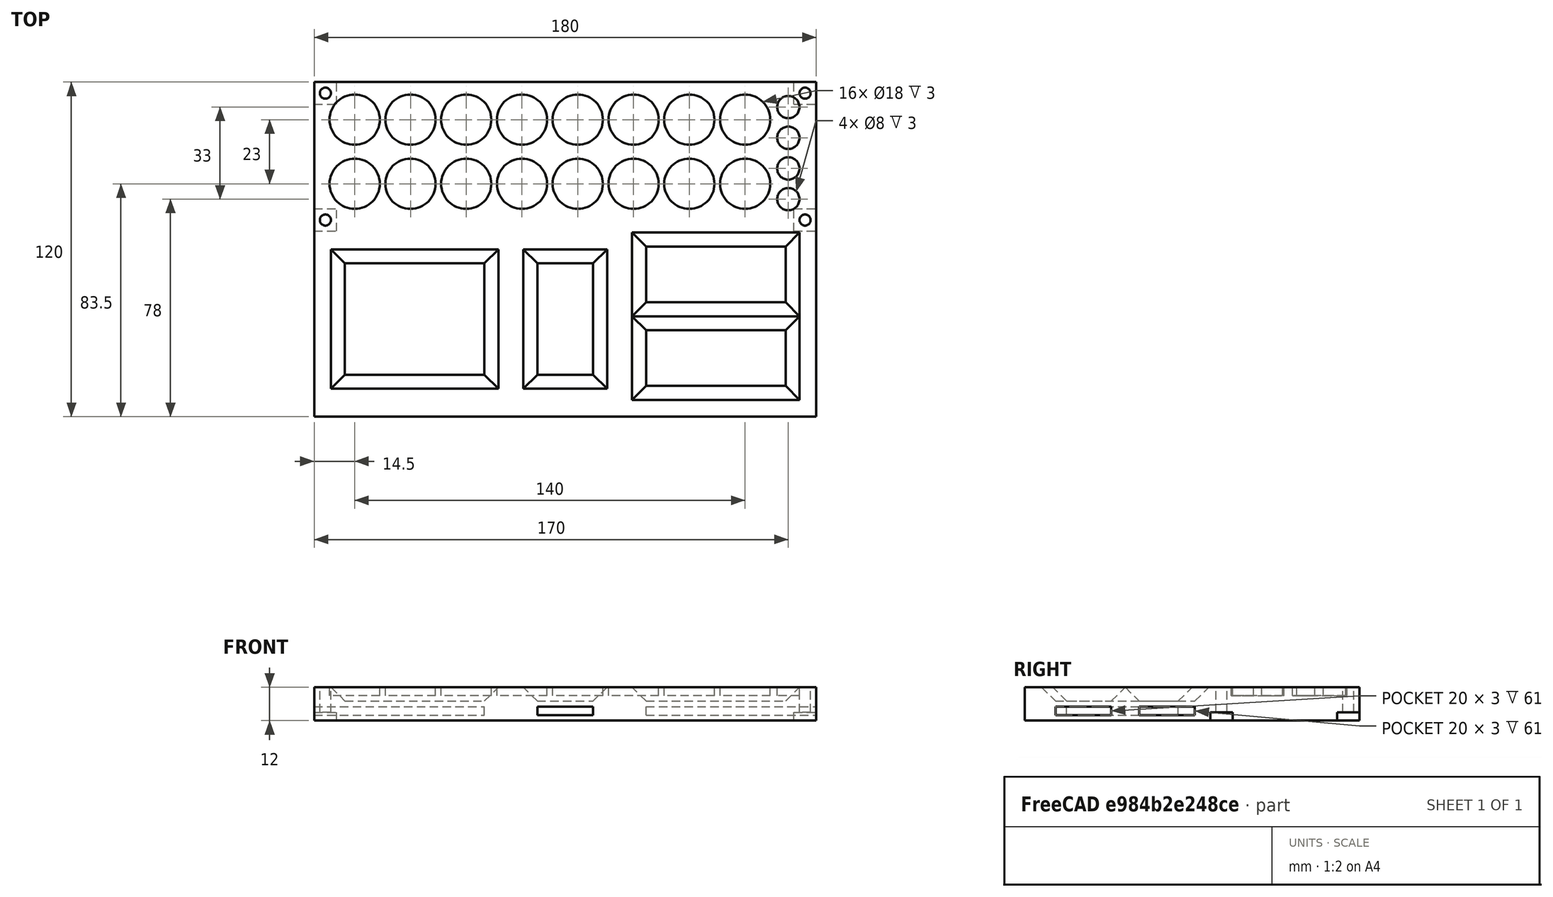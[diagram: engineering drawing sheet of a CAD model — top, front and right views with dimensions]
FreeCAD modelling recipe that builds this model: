
FCSTD DOCUMENT  (FreeCAD 0.17R13509 (Git))
Label: 工具台-1
License: All rights reserved
LicenseURL: http://en.wikipedia.org/wiki/All_rights_reserved
objects: Part::Cut×36, Part::Cylinder×24, Part::Box×9, Part::Feature×4
note: 73 computed .brp shape members not serialized (recipe doc carries the construction recipe); baked Part::Feature solids carry a one-line shape summary decoded from their .brp

FEATURE [Part::Box] Box  label="外壳"
  AttacherType = Attacher::AttachEngine3D
  Height = 12
  Length = 180
  Width = 120
FEATURE [Part::Cylinder] Cylinder  label="圆柱体1.1"
  Angle = 360
  AttacherType = Attacher::AttachEngine3D
  Height = 3
  Placement = pos=(14.5,106.5,9) rot=(0,0,1;0rad)
  Radius = 9
FEATURE [Part::Cylinder] Cylinder001  label="圆柱体1.2"
  Angle = 360
  AttacherType = Attacher::AttachEngine3D
  Height = 3
  Placement = pos=(34.5,106.5,9) rot=(0,0,1;0rad)
  Radius = 9
FEATURE [Part::Cylinder] Cylinder002  label="圆柱体1.3"
  Angle = 360
  AttacherType = Attacher::AttachEngine3D
  Height = 3
  Placement = pos=(54.5,106.5,9) rot=(0,0,1;0rad)
  Radius = 9
FEATURE [Part::Cylinder] Cylinder003  label="圆柱体1.4"
  Angle = 360
  AttacherType = Attacher::AttachEngine3D
  Height = 3
  Placement = pos=(74.5,106.5,9) rot=(0,0,1;0rad)
  Radius = 9
FEATURE [Part::Cylinder] Cylinder004  label="圆柱体2.1"
  Angle = 360
  AttacherType = Attacher::AttachEngine3D
  Height = 3
  Placement = pos=(14.5,83.5,9) rot=(0,0,1;0rad)
  Radius = 9
FEATURE [Part::Cylinder] Cylinder005  label="圆柱体2.2"
  Angle = 360
  AttacherType = Attacher::AttachEngine3D
  Height = 3
  Placement = pos=(34.5,83.5,9) rot=(0,0,1;0rad)
  Radius = 9
FEATURE [Part::Cylinder] Cylinder006  label="圆柱体2.3"
  Angle = 360
  AttacherType = Attacher::AttachEngine3D
  Height = 3
  Placement = pos=(54.5,83.5,9) rot=(0,0,1;0rad)
  Radius = 9
FEATURE [Part::Cylinder] Cylinder007  label="圆柱体2.4"
  Angle = 360
  AttacherType = Attacher::AttachEngine3D
  Height = 3
  Placement = pos=(74.5,83.5,9) rot=(0,0,1;0rad)
  Radius = 9
FEATURE [Part::Feature] Solid  label="梯形1"
  Placement = pos=(6,10,7) rot=(0,0,1;0rad)
  shape: bbox 60 x 50 x 5 mm, 6 faces (baked)
FEATURE [Part::Box] Box001  label="掏空1"
  AttacherType = Attacher::AttachEngine3D
  Height = 3
  Length = 61
  Placement = pos=(0,15,2) rot=(0,0,1;0rad)
  Width = 40
FEATURE [Part::Cylinder] Cylinder008  label="圆柱体1.5"
  Angle = 360
  AttacherType = Attacher::AttachEngine3D
  Height = 3
  Placement = pos=(94.5,106.5,9) rot=(0,0,1;0rad)
  Radius = 9
FEATURE [Part::Cylinder] Cylinder009  label="圆柱体1.6"
  Angle = 360
  AttacherType = Attacher::AttachEngine3D
  Height = 3
  Placement = pos=(114.5,106.5,9) rot=(0,0,1;0rad)
  Radius = 9
FEATURE [Part::Cylinder] Cylinder010  label="圆柱体1.7"
  Angle = 360
  AttacherType = Attacher::AttachEngine3D
  Height = 3
  Placement = pos=(134.5,106.5,9) rot=(0,0,1;0rad)
  Radius = 9
FEATURE [Part::Cylinder] Cylinder011  label="圆柱体1.8"
  Angle = 360
  AttacherType = Attacher::AttachEngine3D
  Height = 3
  Placement = pos=(154.5,106.5,9) rot=(0,0,1;0rad)
  Radius = 9
FEATURE [Part::Cylinder] Cylinder012  label="圆柱体1.9"
  Angle = 360
  AttacherType = Attacher::AttachEngine3D
  Height = 3
  Placement = pos=(170,111,9) rot=(0,0,1;0rad)
  Radius = 4
FEATURE [Part::Cylinder] Cylinder013  label="圆柱体1.10"
  Angle = 360
  AttacherType = Attacher::AttachEngine3D
  Height = 3
  Placement = pos=(170,100,9) rot=(0,0,1;0rad)
  Radius = 4
FEATURE [Part::Cylinder] Cylinder014  label="圆柱体2.5"
  Angle = 360
  AttacherType = Attacher::AttachEngine3D
  Height = 3
  Placement = pos=(94.5,83.5,9) rot=(0,0,1;0rad)
  Radius = 9
FEATURE [Part::Cylinder] Cylinder015  label="圆柱体2.6"
  Angle = 360
  AttacherType = Attacher::AttachEngine3D
  Height = 3
  Placement = pos=(114.5,83.5,9) rot=(0,0,1;0rad)
  Radius = 9
FEATURE [Part::Cylinder] Cylinder016  label="圆柱体2.7"
  Angle = 360
  AttacherType = Attacher::AttachEngine3D
  Height = 3
  Placement = pos=(134.5,83.5,9) rot=(0,0,1;0rad)
  Radius = 9
FEATURE [Part::Cylinder] Cylinder017  label="圆柱体2.8"
  Angle = 360
  AttacherType = Attacher::AttachEngine3D
  Height = 3
  Placement = pos=(154.5,83.5,9) rot=(0,0,1;0rad)
  Radius = 9
FEATURE [Part::Cylinder] Cylinder018  label="圆柱体2.9"
  Angle = 360
  AttacherType = Attacher::AttachEngine3D
  Height = 3
  Placement = pos=(170,89,9) rot=(0,0,1;0rad)
  Radius = 4
FEATURE [Part::Cylinder] Cylinder019  label="圆柱体2.10"
  Angle = 360
  AttacherType = Attacher::AttachEngine3D
  Height = 3
  Placement = pos=(170,78,9) rot=(0,0,1;0rad)
  Radius = 4
FEATURE [Part::Feature] Solid001  label="梯形2"
  Placement = pos=(75,10,7) rot=(0,0,1;0rad)
  shape: bbox 33 x 55 x 5.5 mm, 6 faces (baked)
FEATURE [Part::Feature] Solid002  label="梯形3"
  Placement = pos=(114,6,7) rot=(0,0,1;0rad)
  shape: bbox 66 x 33 x 5.5 mm, 6 faces (baked)
FEATURE [Part::Feature] Solid003  label="梯形4"
  Placement = pos=(114,36,7) rot=(0,0,1;0rad)
  shape: bbox 66 x 33 x 5.5 mm, 6 faces (baked)
FEATURE [Part::Cylinder] Cylinder020  label="螺孔1.1"
  Angle = 360
  AttacherType = Attacher::AttachEngine3D
  Height = 12
  Placement = pos=(4,70.5,0) rot=(0,0,1;0rad)
  Radius = 2
FEATURE [Part::Cylinder] Cylinder021  label="螺孔1.2"
  Angle = 360
  AttacherType = Attacher::AttachEngine3D
  Height = 12
  Placement = pos=(176,70.5,0) rot=(0,0,1;0rad)
  Radius = 2
FEATURE [Part::Cylinder] Cylinder022  label="螺孔1.3"
  Angle = 360
  AttacherType = Attacher::AttachEngine3D
  Height = 12
  Placement = pos=(4,116,0) rot=(0,0,1;0rad)
  Radius = 2
FEATURE [Part::Cylinder] Cylinder023  label="螺孔1.4"
  Angle = 360
  AttacherType = Attacher::AttachEngine3D
  Height = 12
  Placement = pos=(176,116,0) rot=(0,0,1;0rad)
  Radius = 2
FEATURE [Part::Box] Box002  label="掏空2"
  AttacherType = Attacher::AttachEngine3D
  Height = 3
  Length = 20
  Placement = pos=(80,0,2) rot=(0,0,1;0rad)
  Width = 55
FEATURE [Part::Box] Box003  label="掏空3"
  AttacherType = Attacher::AttachEngine3D
  Height = 3
  Length = 61
  Placement = pos=(119,11,2) rot=(0,0,1;0rad)
  Width = 20
FEATURE [Part::Box] Box004  label="掏空4"
  AttacherType = Attacher::AttachEngine3D
  Height = 3
  Length = 61
  Placement = pos=(119,41,2) rot=(0,0,1;0rad)
  Width = 20
FEATURE [Part::Box] Box005  label="螺帽1"
  AttacherType = Attacher::AttachEngine3D
  Height = 3
  Length = 8
  Placement = pos=(0,66.5,0) rot=(0,0,1;0rad)
  Width = 8
FEATURE [Part::Box] Box006  label="螺帽2"
  AttacherType = Attacher::AttachEngine3D
  Height = 3
  Length = 8
  Placement = pos=(172,66.5,0) rot=(0,0,1;0rad)
  Width = 8
FEATURE [Part::Box] Box007  label="螺帽3"
  AttacherType = Attacher::AttachEngine3D
  Height = 3
  Length = 8
  Placement = pos=(0,112,0) rot=(0,0,1;0rad)
  Width = 8
FEATURE [Part::Box] Box008  label="螺帽4"
  AttacherType = Attacher::AttachEngine3D
  Height = 3
  Length = 8
  Placement = pos=(172,112,0) rot=(0,0,1;0rad)
  Width = 8
FEATURE [Part::Cut] Cut
  Base = -> Box
  Tool = -> Cylinder
FEATURE [Part::Cut] Cut001
  Base = -> Cut
  Tool = -> Cylinder001
FEATURE [Part::Cut] Cut002
  Base = -> Cut001
  Tool = -> Cylinder002
FEATURE [Part::Cut] Cut003
  Base = -> Cut002
  Tool = -> Cylinder003
FEATURE [Part::Cut] Cut004
  Base = -> Cut003
  Tool = -> Cylinder004
FEATURE [Part::Cut] Cut005
  Base = -> Cut004
  Tool = -> Cylinder005
FEATURE [Part::Cut] Cut006
  Base = -> Cut005
  Tool = -> Cylinder006
FEATURE [Part::Cut] Cut007
  Base = -> Cut006
  Tool = -> Cylinder007
FEATURE [Part::Cut] Cut008
  Base = -> Cut007
  Tool = -> Solid
FEATURE [Part::Cut] Cut009
  Base = -> Cut008
  Tool = -> Box001
FEATURE [Part::Cut] Cut010
  Base = -> Cut009
  Tool = -> Cylinder008
FEATURE [Part::Cut] Cut011
  Base = -> Cut010
  Tool = -> Cylinder009
FEATURE [Part::Cut] Cut012
  Base = -> Cut011
  Tool = -> Cylinder010
FEATURE [Part::Cut] Cut013
  Base = -> Cut012
  Tool = -> Cylinder011
FEATURE [Part::Cut] Cut014
  Base = -> Cut013
  Tool = -> Cylinder012
FEATURE [Part::Cut] Cut015
  Base = -> Cut014
  Tool = -> Cylinder013
FEATURE [Part::Cut] Cut016
  Base = -> Cut015
  Tool = -> Cylinder014
FEATURE [Part::Cut] Cut017
  Base = -> Cut016
  Tool = -> Cylinder015
FEATURE [Part::Cut] Cut018
  Base = -> Cut017
  Tool = -> Cylinder016
FEATURE [Part::Cut] Cut019
  Base = -> Cut018
  Tool = -> Cylinder017
FEATURE [Part::Cut] Cut020
  Base = -> Cut019
  Tool = -> Cylinder018
FEATURE [Part::Cut] Cut021
  Base = -> Cut020
  Tool = -> Cylinder019
FEATURE [Part::Cut] Cut022
  Base = -> Cut021
  Tool = -> Solid001
FEATURE [Part::Cut] Cut023
  Base = -> Cut022
  Tool = -> Solid002
FEATURE [Part::Cut] Cut024
  Base = -> Cut023
  Tool = -> Solid003
FEATURE [Part::Cut] Cut025
  Base = -> Cut024
  Tool = -> Cylinder020
FEATURE [Part::Cut] Cut026
  Base = -> Cut025
  Tool = -> Cylinder021
FEATURE [Part::Cut] Cut027
  Base = -> Cut026
  Tool = -> Cylinder022
FEATURE [Part::Cut] Cut028
  Base = -> Cut027
  Tool = -> Cylinder023
FEATURE [Part::Cut] Cut029
  Base = -> Cut028
  Tool = -> Box002
FEATURE [Part::Cut] Cut030
  Base = -> Cut029
  Tool = -> Box003
FEATURE [Part::Cut] Cut031
  Base = -> Cut030
  Tool = -> Box004
FEATURE [Part::Cut] Cut032
  Base = -> Cut031
  Tool = -> Box005
FEATURE [Part::Cut] Cut033
  Base = -> Cut032
  Tool = -> Box006
FEATURE [Part::Cut] Cut034
  Base = -> Cut033
  Tool = -> Box007
FEATURE [Part::Cut] Cut035
  Base = -> Cut034
  Tool = -> Box008
